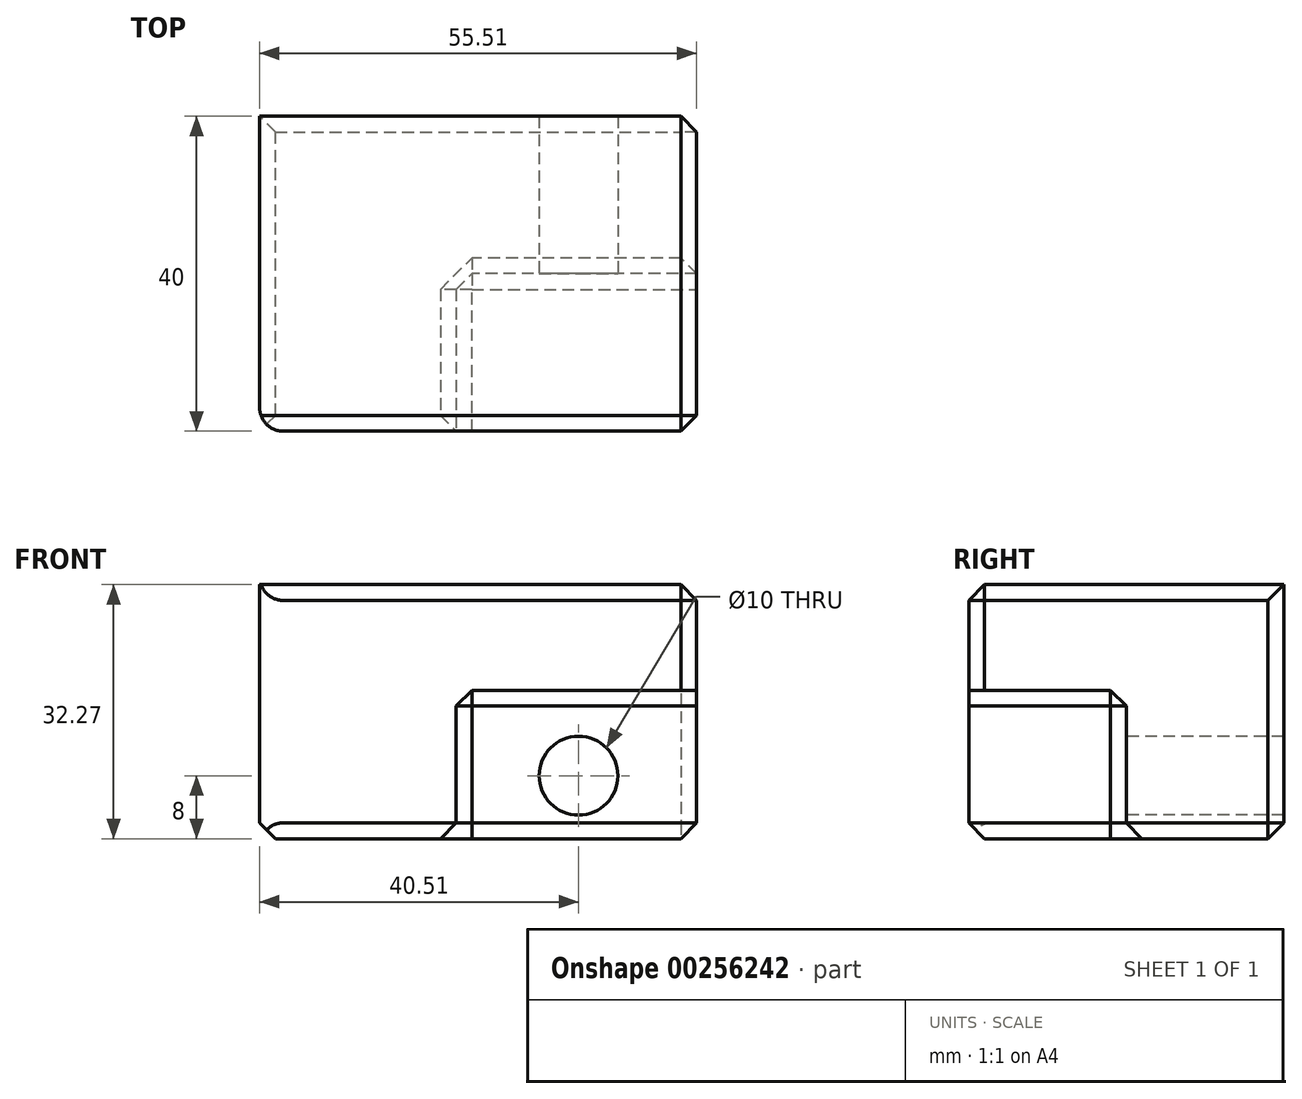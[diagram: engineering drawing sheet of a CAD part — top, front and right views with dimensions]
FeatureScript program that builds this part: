
annotation { "Feature Type Name" : "Feature", "Feature Type Description" : "" }
export const myFeature = defineFeature(function(context is Context, id is Id, definition is map)
    precondition{}
    {
        {
            var Q0;
            Q0=qCreatedBy(makeId("Front.planeOp"),FACE);
            var sketch = newSketch(context, id + "F0", { "sketchPlane" : qUnion([Q0])});
            skLineSegment(sketch, "E0.bottom", {"start": v(0, 0) * mm, "end": v(55.51, 0) * mm});
            skLineSegment(sketch, "E0.top", {"start": v(0, -32.27) * mm, "end": v(55.51, -32.27) * mm});
            skLineSegment(sketch, "E0.left", {"start": v(0, 0) * mm, "end": v(0, -32.27) * mm});
            skLineSegment(sketch, "E0.right", {"start": v(55.51, 0) * mm, "end": v(55.51, -32.27) * mm});
            skSolve(sketch);
        }
        {
            var Q0;
            Q0 = qSketchRegion(id + "F0", true);
            extrude(context, id + "F1", {"entities" : qUnion([Q0]), "depth" : 40 * mm});
        }
        {
            var Q0;
            Q0=makeQuery(id+"F1.opExtrude","CAP_FACE",FACE,{"disambiguationData":[OSD([sQuery(id+"F0.wireOp",EDGE,"E0.bottom"),sQuery(id+"F0.wireOp",EDGE,"E0.top"),sQuery(id+"F0.wireOp",EDGE,"E0.left"),sQuery(id+"F0.wireOp",EDGE,"E0.right")])],"isStart":false});
            var sketch = newSketch(context, id + "F2", { "sketchPlane" : qUnion([Q0])});
            skLineSegment(sketch, "E1.bottom", {"start": v(55.51, -32.27) * mm, "end": v(24.97, -32.27) * mm});
            skLineSegment(sketch, "E1.top", {"start": v(55.51, -13.41) * mm, "end": v(24.97, -13.41) * mm});
            skLineSegment(sketch, "E1.left", {"start": v(55.51, -32.27) * mm, "end": v(55.51, -13.41) * mm});
            skLineSegment(sketch, "E1.right", {"start": v(24.97, -32.27) * mm, "end": v(24.97, -13.41) * mm});
            skSolve(sketch);
        }
        {
            var Q0;
            Q0 = qSketchRegion(id + "F2", true);
            extrude(context, id + "F3", {"entities" : qUnion([Q0]), "operationType" : NewBodyOperationType.REMOVE, "oppositeDirection" : true, "depth" : 20 * mm});
        }
        {
            var Q0;
            Q0=makeQuery(id+"F3.boolean.opBoolean","COPY",FACE,{"derivedFrom":makeQuery(id+"F3.opExtrude","CAP_FACE",FACE,{"disambiguationData":[OSD([sQuery(id+"F2.wireOp",EDGE,"E1.bottom"),sQuery(id+"F2.wireOp",EDGE,"E1.top"),sQuery(id+"F2.wireOp",EDGE,"E1.left"),sQuery(id+"F2.wireOp",EDGE,"E1.right")])],"isStart":false})});
            var sketch = newSketch(context, id + "F4", { "sketchPlane" : qUnion([Q0])});
            skCircle(sketch, "E2", {"center": v(40.51, -24.27) * mm, "radius": 5 * mm});
            skPoint(sketch, "E3", {"position": v(55.51, -24.27) * mm});
            skSolve(sketch);
        }
        {
            var Q0;
            Q0=makeQuery(id+"F4.imprint","IMPRINT",FACE,{"disambiguationData":[TD([[makeQuery(id+"F4.imprint","IMPRINT",EDGE,{"derivedFrom":sQuery(id+"F4.wireOp",EDGE,"E2")}),1.0]])]});
            extrude(context, id + "F5", {"entities" : qUnion([Q0]), "operationType" : NewBodyOperationType.REMOVE, "endBound" : BoundingType.THROUGH_ALL, "oppositeDirection" : true, "depth" : 25 * mm});
        }
        {
            var Q0;
            Q0=makeQuery(id+"F3.boolean.opBoolean","COPY",EDGE,{"derivedFrom":makeQuery(id+"F3.opExtrude","CAP_EDGE",EDGE,{"disambiguationData":[OSD([sQuery(id+"F2.wireOp",EDGE,"E1.right")])],"isStart":true})});
            var Q1;
            Q1=makeQuery(id+"F1.opExtrude","CAP_EDGE",EDGE,{"disambiguationData":[OSD([sQuery(id+"F0.wireOp",EDGE,"E0.top")])],"isStart":false});
            var Q2;
            Q2=makeQuery(id+"F3.boolean.opBoolean","COPY",EDGE,{"derivedFrom":makeQuery(id+"F3.opExtrude","CAP_EDGE",EDGE,{"disambiguationData":[OSD([sQuery(id+"F2.wireOp",EDGE,"E1.top")])],"isStart":true})});
            var Q3;
            Q3=makeQuery(id+"F1.opExtrude","CAP_EDGE",EDGE,{"disambiguationData":[OSD([sQuery(id+"F0.wireOp",EDGE,"E0.bottom")])],"isStart":false});
            var Q4;
            Q4=makeQuery(id+"F1.opExtrude","SWEPT_FACE",FACE,{"disambiguationData":[OSD([sQuery(id+"F0.wireOp",EDGE,"E0.top")])]});
            var Q5;
            Q5=makeQuery(id+"F1.opExtrude","CAP_EDGE",EDGE,{"disambiguationData":[OSD([sQuery(id+"F0.wireOp",EDGE,"E0.top")])],"isStart":true});
            var Q6;
            Q6=makeQuery(id+"F3.boolean.opBoolean","COPY",EDGE,{"derivedFrom":makeQuery(id+"F3.opExtrude","SWEPT_EDGE",EDGE,{"disambiguationData":[OSD([sQuery(id+"F2.wireOp",EDGE,"E1.top"),sQuery(id+"F2.wireOp",EDGE,"E1.right")])]})});
            var Q7;
            Q7=makeQuery(id+"F3.boolean.opBoolean","COPY",EDGE,{"derivedFrom":makeQuery(id+"F3.opExtrude","CAP_EDGE",EDGE,{"disambiguationData":[OSD([sQuery(id+"F2.wireOp",EDGE,"E1.right")])],"isStart":false})});
            var Q8;
            Q8=makeQuery(id+"F3.boolean.opBoolean","COPY",EDGE,{"derivedFrom":makeQuery(id+"F3.opExtrude","CAP_EDGE",EDGE,{"disambiguationData":[OSD([sQuery(id+"F2.wireOp",EDGE,"E1.top")])],"isStart":false})});
            var Q9;
            Q9=makeQuery(id+"F3.boolean.opBoolean","COPY",EDGE,{"derivedFrom":makeQuery(id+"F3.opExtrude","SWEPT_EDGE",EDGE,{"disambiguationData":[OSD([sQuery(id+"F0.wireOp",EDGE,"E0.right"),sQuery(id+"F2.wireOp",EDGE,"E1.top"),sQuery(id+"F2.wireOp",EDGE,"E1.left")])]})});
            var Q10;
            Q10=makeQuery(id+"F3.boolean.opBoolean","COPY",EDGE,{"derivedFrom":makeQuery(id+"F3.opExtrude","CAP_EDGE",EDGE,{"disambiguationData":[OSD([sQuery(id+"F2.wireOp",EDGE,"E1.left")])],"isStart":false})});
            var Q11;
            Q11=makeQuery(id+"F1.opExtrude","CAP_EDGE",EDGE,{"disambiguationData":[OSD([sQuery(id+"F0.wireOp",EDGE,"E0.right")])],"isStart":true});
            var Q12;
            Q12=makeQuery(id+"F1.opExtrude","SWEPT_EDGE",EDGE,{"disambiguationData":[OSD([sQuery(id+"F0.wireOp",EDGE,"E0.bottom"),sQuery(id+"F0.wireOp",EDGE,"E0.right")])]});
            var Q13;
            Q13=makeQuery(id+"F1.opExtrude","CAP_EDGE",EDGE,{"disambiguationData":[OSD([sQuery(id+"F0.wireOp",EDGE,"E0.right")])],"isStart":false});
            chamfer(context, id + "F6", {"entities" : qUnion([Q0, Q1, Q2, Q3, Q4, Q5, Q6, Q7, Q8, Q9, Q10, Q11, Q12, Q13]), "width" : 2 * mm, "tangentPropagation" : true});
        }
        {
            var Q0;
            Q0=makeQuery(id+"F3.boolean.opBoolean","COPY",EDGE,{"derivedFrom":makeQuery(id+"F3.opExtrude","CAP_EDGE",EDGE,{"disambiguationData":[OSD([sQuery(id+"F2.wireOp",EDGE,"E1.right")])],"isStart":true})});
            var Q1;
            Q1=makeQuery(id+"F1.opExtrude","CAP_EDGE",EDGE,{"disambiguationData":[OSD([sQuery(id+"F0.wireOp",EDGE,"E0.left")])],"isStart":false});
            var Q2;
            Q2=makeQuery(id+"F1.opExtrude","CAP_EDGE",EDGE,{"disambiguationData":[OSD([sQuery(id+"F0.wireOp",EDGE,"E0.top")])],"isStart":false});
            var Q3;
            Q3=makeQuery(id+"F3.boolean.opBoolean","COPY",EDGE,{"derivedFrom":makeQuery(id+"F3.opExtrude","CAP_EDGE",EDGE,{"disambiguationData":[OSD([sQuery(id+"F2.wireOp",EDGE,"E1.top")])],"isStart":true})});
            var Q4;
            Q4=makeQuery(id+"F1.opExtrude","CAP_EDGE",EDGE,{"disambiguationData":[OSD([sQuery(id+"F0.wireOp",EDGE,"E0.right")])],"isStart":false});
            var Q5;
            Q5=makeQuery(id+"F1.opExtrude","CAP_EDGE",EDGE,{"disambiguationData":[OSD([sQuery(id+"F0.wireOp",EDGE,"E0.bottom")])],"isStart":false});
            fillet(context, id + "F7", {"entities" : qUnion([Q0, Q1, Q2, Q3, Q4, Q5]), "radius" : 3 * mm, "tangentPropagation" : true, "allowEdgeOverflow" : false});
        }
    });
